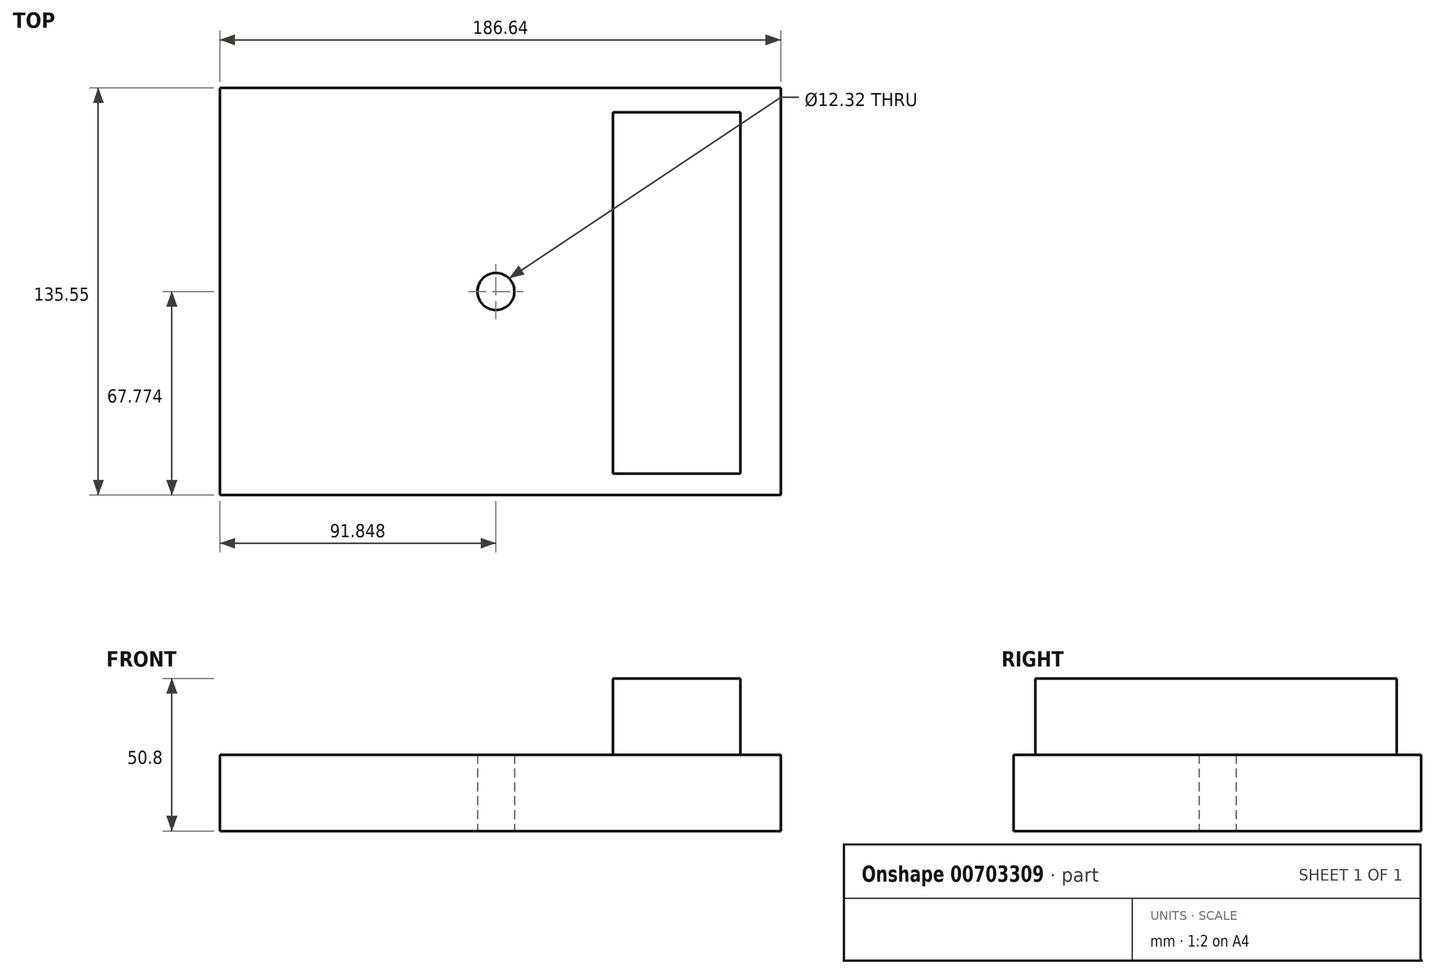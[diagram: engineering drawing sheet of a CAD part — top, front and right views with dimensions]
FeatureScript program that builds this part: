
annotation { "Feature Type Name" : "Feature", "Feature Type Description" : "" }
export const myFeature = defineFeature(function(context is Context, id is Id, definition is map)
    precondition{}
    {
        {
            var Q0;
            Q0=qCreatedBy(makeId("Top.planeOp"),FACE);
            var sketch = newSketch(context, id + "F0", { "sketchPlane" : qUnion([Q0])});
            skLineSegment(sketch, "E0.bottom", {"start": v(-112.46, 105.24) * mm, "end": v(74.18, 105.24) * mm});
            skLineSegment(sketch, "E0.top", {"start": v(-112.46, -30.31) * mm, "end": v(74.18, -30.31) * mm});
            skLineSegment(sketch, "E0.left", {"start": v(-112.46, 105.24) * mm, "end": v(-112.46, -30.31) * mm});
            skLineSegment(sketch, "E0.right", {"start": v(74.18, 105.24) * mm, "end": v(74.18, -30.31) * mm});
            skCircle(sketch, "E1", {"center": v(-20.61, 37.46) * mm, "radius": 6.16 * mm});
            skPoint(sketch, "E1.centerSnap0", {"position": v(-112.46, 37.46) * mm});
            skSolve(sketch);
        }
        {
            var Q0;
            Q0=makeQuery(id+"F0.imprint","IMPRINT",FACE,{"disambiguationData":[TD([[makeQuery(id+"F0.imprint","IMPRINT",EDGE,{"derivedFrom":sQuery(id+"F0.wireOp",EDGE,"E0.bottom")}),-1.0]])]});
            extrude(context, id + "F1", {"entities" : qUnion([Q0]), "depth" : 25.4 * mm, "offsetDistance" : 25.4 * mm});
        }
        {
            var Q0;
            Q0=makeQuery(id+"F1.opExtrude","CAP_FACE",FACE,{"disambiguationData":[OSD([sQuery(id+"F0.wireOp",EDGE,"E0.bottom"),sQuery(id+"F0.wireOp",EDGE,"E0.top"),sQuery(id+"F0.wireOp",EDGE,"E0.left"),sQuery(id+"F0.wireOp",EDGE,"E0.right"),sQuery(id+"F0.wireOp",EDGE,"E1")])],"isStart":false});
            var sketch = newSketch(context, id + "F2", { "sketchPlane" : qUnion([Q0])});
            skLineSegment(sketch, "E2.bottom", {"start": v(60.77, 97.17) * mm, "end": v(18.35, 97.17) * mm});
            skLineSegment(sketch, "E2.top", {"start": v(60.77, -23.13) * mm, "end": v(18.35, -23.13) * mm});
            skLineSegment(sketch, "E2.left", {"start": v(60.77, 97.17) * mm, "end": v(60.77, -23.13) * mm});
            skLineSegment(sketch, "E2.right", {"start": v(18.35, 97.17) * mm, "end": v(18.35, -23.13) * mm});
            skSolve(sketch);
        }
        {
            var Q0;
            Q0=makeQuery(id+"F2.imprint","IMPRINT",FACE,{"disambiguationData":[TD([[makeQuery(id+"F2.imprint","IMPRINT",EDGE,{"derivedFrom":sQuery(id+"F2.wireOp",EDGE,"E2.bottom")}),1.0]])]});
            extrude(context, id + "F3", {"entities" : qUnion([Q0]), "operationType" : NewBodyOperationType.ADD, "depth" : 25.4 * mm, "offsetDistance" : 25.4 * mm});
        }
    });
